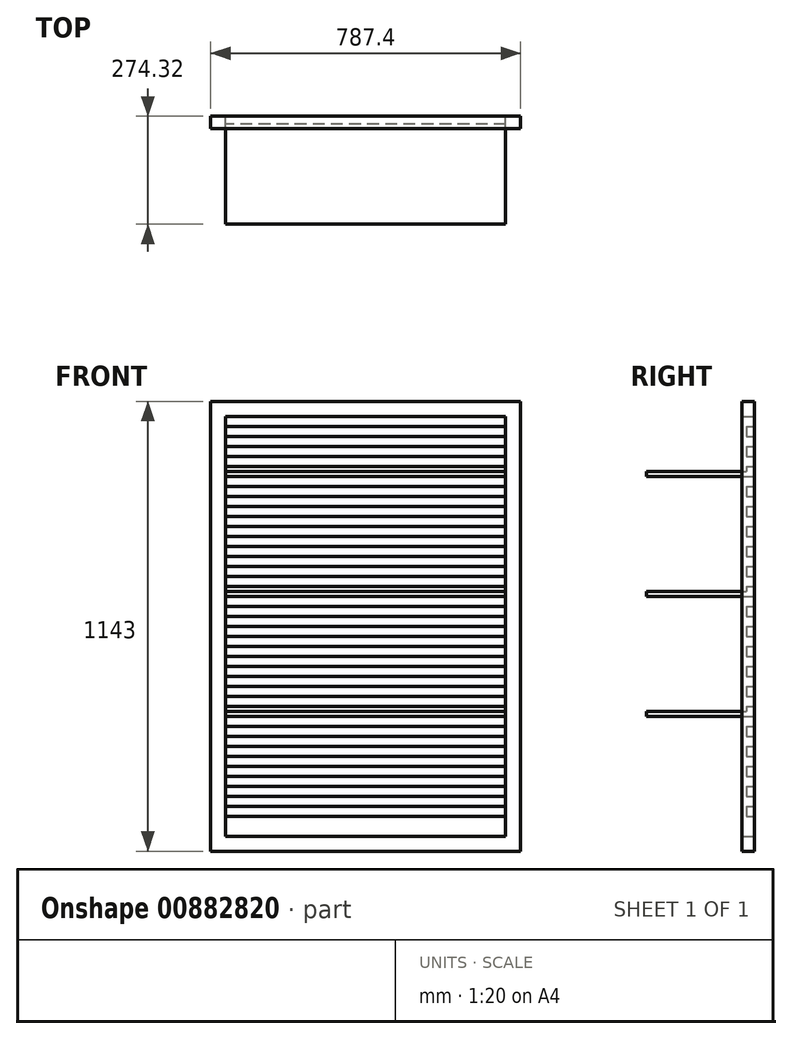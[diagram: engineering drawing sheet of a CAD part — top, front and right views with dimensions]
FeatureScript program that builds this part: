
annotation { "Feature Type Name" : "Feature", "Feature Type Description" : "" }
export const myFeature = defineFeature(function(context is Context, id is Id, definition is map)
    precondition{}
    {
        {
            var Q0;
            Q0=qCreatedBy(makeId("Front.planeOp"),FACE);
            var sketch = newSketch(context, id + "F0", { "sketchPlane" : qUnion([Q0])});
            skLineSegment(sketch, "E0.bottom", {"start": v(-393.7, 571.5) * mm, "end": v(393.7, 571.5) * mm});
            skLineSegment(sketch, "E0.top", {"start": v(-393.7, -571.5) * mm, "end": v(393.7, -571.5) * mm});
            skLineSegment(sketch, "E0.left", {"start": v(-393.7, 571.5) * mm, "end": v(-393.7, -571.5) * mm});
            skLineSegment(sketch, "E0.right", {"start": v(393.7, 571.5) * mm, "end": v(393.7, -571.5) * mm});
            skPoint(sketch, "E0.middle", {"position": v(0, 0) * mm});
            skLineSegment(sketch, "E1.0", {"start": v(-355.6, -533.4) * mm, "end": v(355.6, -533.4) * mm});
            skLineSegment(sketch, "E1.1", {"start": v(-355.6, 533.4) * mm, "end": v(-355.6, -533.4) * mm});
            skLineSegment(sketch, "E1.2", {"start": v(-355.6, 533.4) * mm, "end": v(355.6, 533.4) * mm});
            skLineSegment(sketch, "E1.3", {"start": v(355.6, 533.4) * mm, "end": v(355.6, -533.4) * mm});
            skSolve(sketch);
        }
        {
            var Q0;
            Q0 = qSketchRegion(id + "F0", true);
            extrude(context, id + "F1", {"entities" : qUnion([Q0]), "depth" : 31.75 * mm, "offsetDistance" : 25.4 * mm});
        }
        {
            var Q0;
            Q0=makeQuery(id+"F1.opExtrude","CAP_FACE",FACE,{"disambiguationData":[OSD([sQuery(id+"F0.wireOp",EDGE,"E0.bottom"),sQuery(id+"F0.wireOp",EDGE,"E0.top"),sQuery(id+"F0.wireOp",EDGE,"E0.left"),sQuery(id+"F0.wireOp",EDGE,"E0.right"),sQuery(id+"F0.wireOp",EDGE,"E1.0"),sQuery(id+"F0.wireOp",EDGE,"E1.1"),sQuery(id+"F0.wireOp",EDGE,"E1.2"),sQuery(id+"F0.wireOp",EDGE,"E1.3")])],"isStart":true});
            var sketch = newSketch(context, id + "F2", { "sketchPlane" : qUnion([Q0])});
            skLineSegment(sketch, "E2.bottom", {"start": v(-355.6, 508) * mm, "end": v(355.6, 508) * mm});
            skLineSegment(sketch, "E2.top", {"start": v(-355.6, 482.6) * mm, "end": v(355.6, 482.6) * mm});
            skLineSegment(sketch, "E2.left", {"start": v(-355.6, 508) * mm, "end": v(-355.6, 482.6) * mm});
            skLineSegment(sketch, "E2.right", {"start": v(355.6, 508) * mm, "end": v(355.6, 482.6) * mm});
            skLineSegment(sketch, "E3.0.1.0", {"start": v(-355.6, 457.2) * mm, "end": v(355.6, 457.2) * mm});
            skLineSegment(sketch, "E3.0.1.1", {"start": v(-355.6, 431.8) * mm, "end": v(355.6, 431.8) * mm});
            skLineSegment(sketch, "E3.0.1.2", {"start": v(-355.6, 457.2) * mm, "end": v(-355.6, 431.8) * mm});
            skLineSegment(sketch, "E3.0.1.3", {"start": v(355.6, 457.2) * mm, "end": v(355.6, 431.8) * mm});
            skLineSegment(sketch, "E3.0.2.0", {"start": v(-355.6, 406.4) * mm, "end": v(355.6, 406.4) * mm});
            skLineSegment(sketch, "E3.0.2.1", {"start": v(-355.6, 381) * mm, "end": v(355.6, 381) * mm});
            skLineSegment(sketch, "E3.0.2.2", {"start": v(-355.6, 406.4) * mm, "end": v(-355.6, 381) * mm});
            skLineSegment(sketch, "E3.0.2.3", {"start": v(355.6, 406.4) * mm, "end": v(355.6, 381) * mm});
            skLineSegment(sketch, "E3.0.3.0", {"start": v(-355.6, 355.6) * mm, "end": v(355.6, 355.6) * mm});
            skLineSegment(sketch, "E3.0.3.1", {"start": v(-355.6, 330.2) * mm, "end": v(355.6, 330.2) * mm});
            skLineSegment(sketch, "E3.0.3.2", {"start": v(-355.6, 355.6) * mm, "end": v(-355.6, 330.2) * mm});
            skLineSegment(sketch, "E3.0.3.3", {"start": v(355.6, 355.6) * mm, "end": v(355.6, 330.2) * mm});
            skLineSegment(sketch, "E3.0.4.0", {"start": v(-355.6, 304.8) * mm, "end": v(355.6, 304.8) * mm});
            skLineSegment(sketch, "E3.0.4.1", {"start": v(-355.6, 279.4) * mm, "end": v(355.6, 279.4) * mm});
            skLineSegment(sketch, "E3.0.4.2", {"start": v(-355.6, 304.8) * mm, "end": v(-355.6, 279.4) * mm});
            skLineSegment(sketch, "E3.0.4.3", {"start": v(355.6, 304.8) * mm, "end": v(355.6, 279.4) * mm});
            skLineSegment(sketch, "E3.0.5.0", {"start": v(-355.6, 254) * mm, "end": v(355.6, 254) * mm});
            skLineSegment(sketch, "E3.0.5.1", {"start": v(-355.6, 228.6) * mm, "end": v(355.6, 228.6) * mm});
            skLineSegment(sketch, "E3.0.5.2", {"start": v(-355.6, 254) * mm, "end": v(-355.6, 228.6) * mm});
            skLineSegment(sketch, "E3.0.5.3", {"start": v(355.6, 254) * mm, "end": v(355.6, 228.6) * mm});
            skLineSegment(sketch, "E3.0.6.0", {"start": v(-355.6, 203.2) * mm, "end": v(355.6, 203.2) * mm});
            skLineSegment(sketch, "E3.0.6.1", {"start": v(-355.6, 177.8) * mm, "end": v(355.6, 177.8) * mm});
            skLineSegment(sketch, "E3.0.6.2", {"start": v(-355.6, 203.2) * mm, "end": v(-355.6, 177.8) * mm});
            skLineSegment(sketch, "E3.0.6.3", {"start": v(355.6, 203.2) * mm, "end": v(355.6, 177.8) * mm});
            skLineSegment(sketch, "E3.0.7.0", {"start": v(-355.6, 152.4) * mm, "end": v(355.6, 152.4) * mm});
            skLineSegment(sketch, "E3.0.7.1", {"start": v(-355.6, 127) * mm, "end": v(355.6, 127) * mm});
            skLineSegment(sketch, "E3.0.7.2", {"start": v(-355.6, 152.4) * mm, "end": v(-355.6, 127) * mm});
            skLineSegment(sketch, "E3.0.7.3", {"start": v(355.6, 152.4) * mm, "end": v(355.6, 127) * mm});
            skLineSegment(sketch, "E3.0.8.0", {"start": v(-355.6, 101.6) * mm, "end": v(355.6, 101.6) * mm});
            skLineSegment(sketch, "E3.0.8.1", {"start": v(-355.6, 76.2) * mm, "end": v(355.6, 76.2) * mm});
            skLineSegment(sketch, "E3.0.8.2", {"start": v(-355.6, 101.6) * mm, "end": v(-355.6, 76.2) * mm});
            skLineSegment(sketch, "E3.0.8.3", {"start": v(355.6, 101.6) * mm, "end": v(355.6, 76.2) * mm});
            skLineSegment(sketch, "E3.0.9.0", {"start": v(-355.6, 50.8) * mm, "end": v(355.6, 50.8) * mm});
            skLineSegment(sketch, "E3.0.9.1", {"start": v(-355.6, 25.4) * mm, "end": v(355.6, 25.4) * mm});
            skLineSegment(sketch, "E3.0.9.2", {"start": v(-355.6, 50.8) * mm, "end": v(-355.6, 25.4) * mm});
            skLineSegment(sketch, "E3.0.9.3", {"start": v(355.6, 50.8) * mm, "end": v(355.6, 25.4) * mm});
            skLineSegment(sketch, "E3.0.10.0", {"start": v(-355.6, 0) * mm, "end": v(355.6, 0) * mm});
            skLineSegment(sketch, "E3.0.10.1", {"start": v(-355.6, -25.4) * mm, "end": v(355.6, -25.4) * mm});
            skLineSegment(sketch, "E3.0.10.2", {"start": v(-355.6, 0) * mm, "end": v(-355.6, -25.4) * mm});
            skLineSegment(sketch, "E3.0.10.3", {"start": v(355.6, 0) * mm, "end": v(355.6, -25.4) * mm});
            skLineSegment(sketch, "E3.0.11.0", {"start": v(-355.6, -50.8) * mm, "end": v(355.6, -50.8) * mm});
            skLineSegment(sketch, "E3.0.11.1", {"start": v(-355.6, -76.2) * mm, "end": v(355.6, -76.2) * mm});
            skLineSegment(sketch, "E3.0.11.2", {"start": v(-355.6, -50.8) * mm, "end": v(-355.6, -76.2) * mm});
            skLineSegment(sketch, "E3.0.11.3", {"start": v(355.6, -50.8) * mm, "end": v(355.6, -76.2) * mm});
            skLineSegment(sketch, "E3.0.12.0", {"start": v(-355.6, -101.6) * mm, "end": v(355.6, -101.6) * mm});
            skLineSegment(sketch, "E3.0.12.1", {"start": v(-355.6, -127) * mm, "end": v(355.6, -127) * mm});
            skLineSegment(sketch, "E3.0.12.2", {"start": v(-355.6, -101.6) * mm, "end": v(-355.6, -127) * mm});
            skLineSegment(sketch, "E3.0.12.3", {"start": v(355.6, -101.6) * mm, "end": v(355.6, -127) * mm});
            skLineSegment(sketch, "E3.0.13.0", {"start": v(-355.6, -152.4) * mm, "end": v(355.6, -152.4) * mm});
            skLineSegment(sketch, "E3.0.13.1", {"start": v(-355.6, -177.8) * mm, "end": v(355.6, -177.8) * mm});
            skLineSegment(sketch, "E3.0.13.2", {"start": v(-355.6, -152.4) * mm, "end": v(-355.6, -177.8) * mm});
            skLineSegment(sketch, "E3.0.13.3", {"start": v(355.6, -152.4) * mm, "end": v(355.6, -177.8) * mm});
            skLineSegment(sketch, "E3.0.14.0", {"start": v(-355.6, -203.2) * mm, "end": v(355.6, -203.2) * mm});
            skLineSegment(sketch, "E3.0.14.1", {"start": v(-355.6, -228.6) * mm, "end": v(355.6, -228.6) * mm});
            skLineSegment(sketch, "E3.0.14.2", {"start": v(-355.6, -203.2) * mm, "end": v(-355.6, -228.6) * mm});
            skLineSegment(sketch, "E3.0.14.3", {"start": v(355.6, -203.2) * mm, "end": v(355.6, -228.6) * mm});
            skLineSegment(sketch, "E3.0.15.0", {"start": v(-355.6, -254) * mm, "end": v(355.6, -254) * mm});
            skLineSegment(sketch, "E3.0.15.1", {"start": v(-355.6, -279.4) * mm, "end": v(355.6, -279.4) * mm});
            skLineSegment(sketch, "E3.0.15.2", {"start": v(-355.6, -254) * mm, "end": v(-355.6, -279.4) * mm});
            skLineSegment(sketch, "E3.0.15.3", {"start": v(355.6, -254) * mm, "end": v(355.6, -279.4) * mm});
            skLineSegment(sketch, "E3.0.16.0", {"start": v(-355.6, -304.8) * mm, "end": v(355.6, -304.8) * mm});
            skLineSegment(sketch, "E3.0.16.1", {"start": v(-355.6, -330.2) * mm, "end": v(355.6, -330.2) * mm});
            skLineSegment(sketch, "E3.0.16.2", {"start": v(-355.6, -304.8) * mm, "end": v(-355.6, -330.2) * mm});
            skLineSegment(sketch, "E3.0.16.3", {"start": v(355.6, -304.8) * mm, "end": v(355.6, -330.2) * mm});
            skLineSegment(sketch, "E3.0.17.0", {"start": v(-355.6, -355.6) * mm, "end": v(355.6, -355.6) * mm});
            skLineSegment(sketch, "E3.0.17.1", {"start": v(-355.6, -381) * mm, "end": v(355.6, -381) * mm});
            skLineSegment(sketch, "E3.0.17.2", {"start": v(-355.6, -355.6) * mm, "end": v(-355.6, -381) * mm});
            skLineSegment(sketch, "E3.0.17.3", {"start": v(355.6, -355.6) * mm, "end": v(355.6, -381) * mm});
            skLineSegment(sketch, "E3.0.18.0", {"start": v(-355.6, -406.4) * mm, "end": v(355.6, -406.4) * mm});
            skLineSegment(sketch, "E3.0.18.1", {"start": v(-355.6, -431.8) * mm, "end": v(355.6, -431.8) * mm});
            skLineSegment(sketch, "E3.0.18.2", {"start": v(-355.6, -406.4) * mm, "end": v(-355.6, -431.8) * mm});
            skLineSegment(sketch, "E3.0.18.3", {"start": v(355.6, -406.4) * mm, "end": v(355.6, -431.8) * mm});
            skLineSegment(sketch, "E3.0.19.0", {"start": v(-355.6, -457.2) * mm, "end": v(355.6, -457.2) * mm});
            skLineSegment(sketch, "E3.0.19.1", {"start": v(-355.6, -482.6) * mm, "end": v(355.6, -482.6) * mm});
            skLineSegment(sketch, "E3.0.19.2", {"start": v(-355.6, -457.2) * mm, "end": v(-355.6, -482.6) * mm});
            skLineSegment(sketch, "E3.0.19.3", {"start": v(355.6, -457.2) * mm, "end": v(355.6, -482.6) * mm});
            skLineSegment(sketch, "E3.direction1", {"start": v(-355.6, 482.6) * mm, "end": v(-330.2, 482.6) * mm, "construction": true});
            skLineSegment(sketch, "E3.direction2", {"start": v(-355.6, 482.6) * mm, "end": v(-355.6, 431.8) * mm, "construction": true});
            skSolve(sketch);
        }
        {
            var Q0;
            Q0 = qSketchRegion(id + "F2", true);
            extrude(context, id + "F3", {"entities" : qUnion([Q0]), "operationType" : NewBodyOperationType.ADD, "oppositeDirection" : true, "depth" : 20.32 * mm, "offsetDistance" : 25.4 * mm});
        }
        {
            var Q0;
            Q0=makeQuery(id+"F3.opExtrude","CAP_FACE",FACE,{"disambiguationData":[OSD([sQuery(id+"F2.wireOp",EDGE,"E3.0.2.0"),sQuery(id+"F2.wireOp",EDGE,"E3.0.2.1"),sQuery(id+"F2.wireOp",EDGE,"E3.0.2.2"),sQuery(id+"F2.wireOp",EDGE,"E3.0.2.3")])],"isStart":false});
            var sketch = newSketch(context, id + "F4", { "sketchPlane" : qUnion([Q0])});
            skLineSegment(sketch, "E4.bottom", {"start": v(-355.6, 381) * mm, "end": v(355.6, 381) * mm});
            skLineSegment(sketch, "E4.top", {"start": v(-355.6, 393.7) * mm, "end": v(355.6, 393.7) * mm});
            skLineSegment(sketch, "E4.left", {"start": v(-355.6, 381) * mm, "end": v(-355.6, 393.7) * mm});
            skLineSegment(sketch, "E4.right", {"start": v(355.6, 381) * mm, "end": v(355.6, 393.7) * mm});
            skLineSegment(sketch, "E5.0.1.0", {"start": v(-355.6, 76.2) * mm, "end": v(355.6, 76.2) * mm});
            skLineSegment(sketch, "E5.0.1.1", {"start": v(-355.6, 88.9) * mm, "end": v(355.6, 88.9) * mm});
            skLineSegment(sketch, "E5.0.1.2", {"start": v(-355.6, 76.2) * mm, "end": v(-355.6, 88.9) * mm});
            skLineSegment(sketch, "E5.0.1.3", {"start": v(355.6, 76.2) * mm, "end": v(355.6, 88.9) * mm});
            skLineSegment(sketch, "E5.0.2.0", {"start": v(-355.6, -228.6) * mm, "end": v(355.6, -228.6) * mm});
            skLineSegment(sketch, "E5.0.2.1", {"start": v(-355.6, -215.9) * mm, "end": v(355.6, -215.9) * mm});
            skLineSegment(sketch, "E5.0.2.2", {"start": v(-355.6, -228.6) * mm, "end": v(-355.6, -215.9) * mm});
            skLineSegment(sketch, "E5.0.2.3", {"start": v(355.6, -228.6) * mm, "end": v(355.6, -215.9) * mm});
            skLineSegment(sketch, "E5.direction1", {"start": v(-355.6, 381) * mm, "end": v(-330.2, 381) * mm, "construction": true});
            skLineSegment(sketch, "E5.direction2", {"start": v(-355.6, 381) * mm, "end": v(-355.6, 76.2) * mm, "construction": true});
            skSolve(sketch);
        }
        {
            var Q0;
            Q0 = qSketchRegion(id + "F4", true);
            extrude(context, id + "F5", {"entities" : qUnion([Q0]), "operationType" : NewBodyOperationType.ADD, "depth" : 254 * mm, "offsetDistance" : 25.4 * mm});
        }
    });
